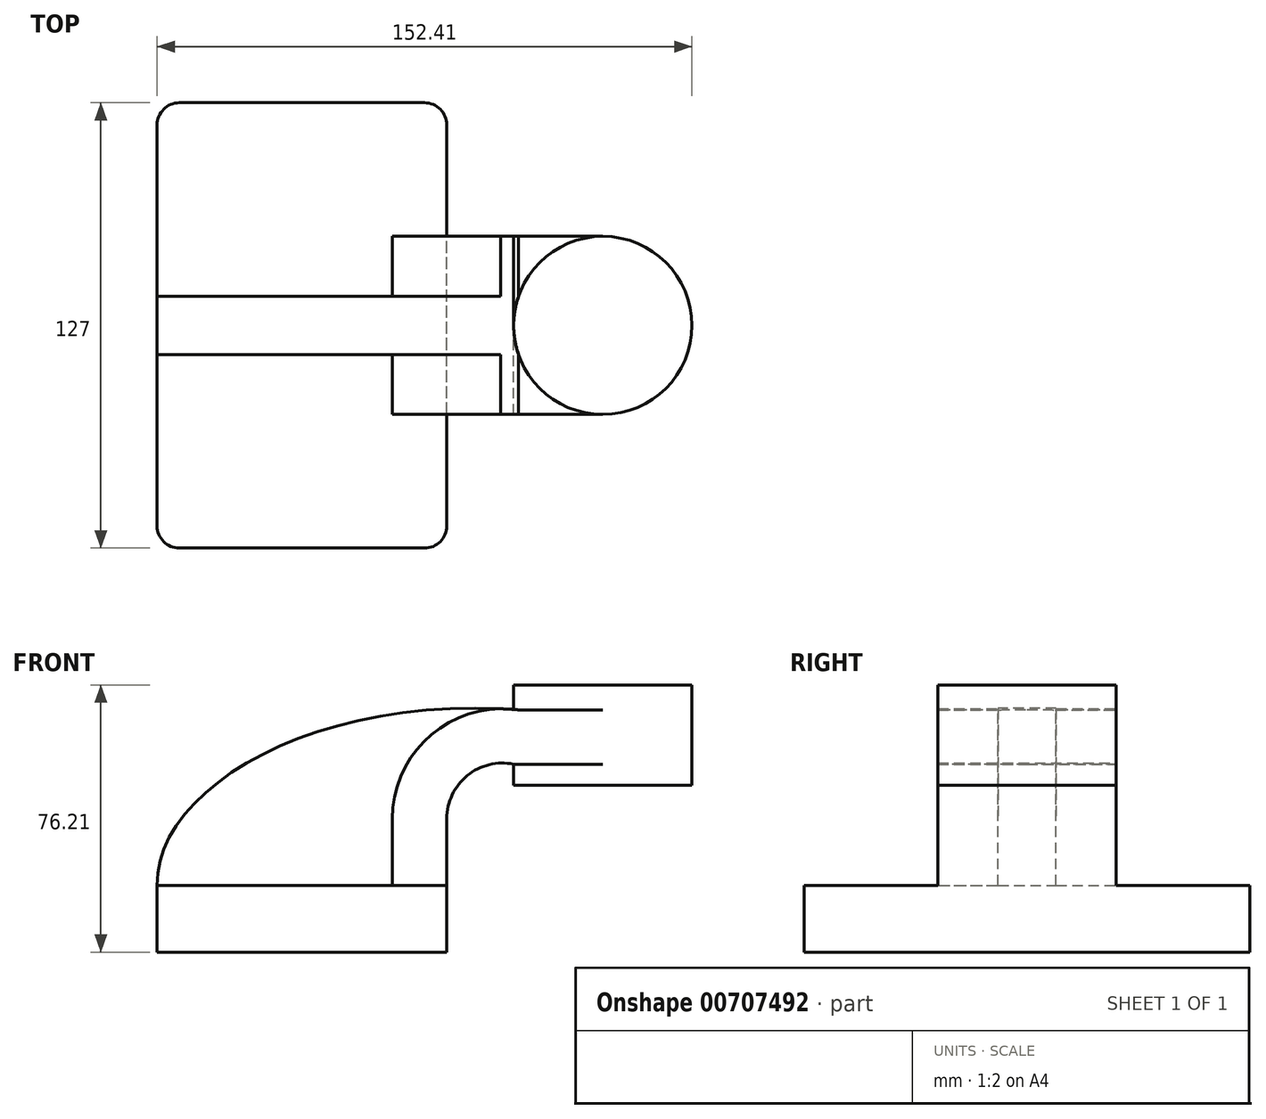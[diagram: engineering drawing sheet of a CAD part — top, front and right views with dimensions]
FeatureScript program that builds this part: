
annotation { "Feature Type Name" : "Feature", "Feature Type Description" : "" }
export const myFeature = defineFeature(function(context is Context, id is Id, definition is map)
    precondition{}
    {
        {
            var Q0;
            Q0=qCreatedBy(makeId("Front.planeOp"),FACE);
            var sketch = newSketch(context, id + "F0", { "sketchPlane" : qUnion([Q0])});
            skLineSegment(sketch, "E0.bottom", {"start": v(41.28, -9.52) * mm, "end": v(-41.28, -9.52) * mm});
            skLineSegment(sketch, "E0.top", {"start": v(41.28, 9.53) * mm, "end": v(-41.28, 9.53) * mm});
            skLineSegment(sketch, "E0.left", {"start": v(41.28, -9.52) * mm, "end": v(41.28, 9.53) * mm});
            skLineSegment(sketch, "E0.right", {"start": v(-41.28, -9.52) * mm, "end": v(-41.28, 9.53) * mm});
            skPoint(sketch, "E0.middle", {"position": v(0, 0) * mm});
            skLineSegment(sketch, "E1.bottom", {"start": v(111.12, 38.1) * mm, "end": v(60.32, 38.1) * mm});
            skLineSegment(sketch, "E1.top", {"start": v(111.12, 66.68) * mm, "end": v(60.32, 66.68) * mm});
            skLineSegment(sketch, "E1.left", {"start": v(111.12, 38.1) * mm, "end": v(111.12, 66.68) * mm});
            skLineSegment(sketch, "E1.right", {"start": v(60.32, 38.1) * mm, "end": v(60.32, 66.68) * mm});
            skPoint(sketch, "E1.middle", {"position": v(85.72, 52.39) * mm});
            skLineSegment(sketch, "E2", {"start": v(41.28, 9.53) * mm, "end": v(41.28, 28.5) * mm});
            skArc(sketch, "E3", {"start": v(41.28, 28.5) * mm, "mid": v(47.1, 40.8) * mm, "end": v(60.32, 44.06) * mm});
            skLineSegment(sketch, "E4", {"start": v(60.32, 44.06) * mm, "end": v(85.72, 44.06) * mm});
            skLineSegment(sketch, "E5", {"start": v(85.73, 66.68) * mm, "end": v(85.73, 38.1) * mm});
            skPoint(sketch, "E6", {"position": v(85.72, 38.1) * mm});
            skLineSegment(sketch, "E7.0", {"start": v(61.62, 59.55) * mm, "end": v(85.72, 59.55) * mm});
            skArc(sketch, "E7.1", {"start": v(25.78, 28.5) * mm, "mid": v(36.61, 52.22) * mm, "end": v(61.62, 59.55) * mm});
            skLineSegment(sketch, "E7.2", {"start": v(25.78, 9.53) * mm, "end": v(25.78, 28.5) * mm});
            skFitSpline(sketch, "E8", {"points": [v(-41.28, 9.52) * mm, v(61.62, 59.55) * mm], "startDerivative": vector(-1.83, 81.78) * mm, "endDerivative": vector(175.47, -13.6) * mm});
            skSolve(sketch);
        }
        {
            var Q0;
            Q0=makeQuery(id+"F0.imprint","IMPRINT",FACE,{"disambiguationData":[TD([[makeQuery(id+"F0.imprint","IMPRINT",EDGE,{"derivedFrom":sQuery(id+"F0.wireOp",EDGE,"E0.bottom")}),-1.0]])]});
            extrude(context, id + "F1", {"entities" : qUnion([Q0]), "endBound" : BoundingType.SYMMETRIC, "depth" : 127 * mm, "offsetDistance" : 25.4 * mm});
        }
        {
            var Q0;
            {var subQ1=sQuery(id+"F0.wireOp",EDGE,"E2");Q0=makeQuery(id+"F0.imprint","IMPRINT",FACE,{"disambiguationData":[TD([[makeQuery(id+"F0.imprint","IMPRINT",EDGE,{"derivedFrom":subQ1}),1.0]])]});}
            var Q1;
            {var subQ2=sQuery(id+"F0.wireOp",EDGE,"E4");Q1=makeQuery(id+"F0.imprint","IMPRINT",FACE,{"disambiguationData":[TD([[makeQuery(id+"F0.imprint","IMPRINT",EDGE,{"derivedFrom":subQ2}),1.0]])]});}
            extrude(context, id + "F2", {"entities" : qUnion([Q0, Q1]), "operationType" : NewBodyOperationType.ADD, "endBound" : BoundingType.SYMMETRIC, "depth" : 50.8 * mm, "offsetDistance" : 25.4 * mm});
        }
        {
            var Q0;
            {var subQ0=sQuery(id+"F0.wireOp",EDGE,"E7.2");Q0=makeQuery(id+"F0.imprint","IMPRINT",FACE,{"disambiguationData":[TD([[makeQuery(id+"F0.imprint","IMPRINT",EDGE,{"derivedFrom":subQ0}),1.0]])]});}
            extrude(context, id + "F3", {"entities" : qUnion([Q0]), "operationType" : NewBodyOperationType.ADD, "endBound" : BoundingType.SYMMETRIC, "depth" : 16.56 * mm, "offsetDistance" : 25.4 * mm});
        }
        {
            var Q0;
            {var subQ0=sQuery(id+"F0.wireOp",EDGE,"E1.left");Q0=makeQuery(id+"F0.imprint","IMPRINT",FACE,{"disambiguationData":[TD([[makeQuery(id+"F0.imprint","IMPRINT",EDGE,{"derivedFrom":subQ0}),1.0]])]});}
            var Q1;
            Q1=sQuery(id+"F0.wireOp",EDGE,"E5");
            revolve(context, id + "F4", {"operationType" : NewBodyOperationType.ADD, "surfaceOperationType" : NewSurfaceOperationType.NEW, "entities" : qUnion([Q0]), "axis" : qUnion([Q1]), "revolveType" : RevolveType.FULL});
        }
        {
            var Q0;
            Q0=makeQuery(id+"F1.opExtrude","CAP_EDGE",EDGE,{"disambiguationData":[OSD([sQuery(id+"F0.wireOp",EDGE,"E0.left")])],"isStart":false});
            var Q1;
            Q1=makeQuery(id+"F1.opExtrude","CAP_EDGE",EDGE,{"disambiguationData":[OSD([sQuery(id+"F0.wireOp",EDGE,"E0.right")])],"isStart":false});
            var Q2;
            Q2=makeQuery(id+"F1.opExtrude","CAP_EDGE",EDGE,{"disambiguationData":[OSD([sQuery(id+"F0.wireOp",EDGE,"E0.right")])],"isStart":true});
            var Q3;
            Q3=makeQuery(id+"F1.opExtrude","CAP_EDGE",EDGE,{"disambiguationData":[OSD([sQuery(id+"F0.wireOp",EDGE,"E0.left")])],"isStart":true});
            fillet(context, id + "F5", {"entities" : qUnion([Q0, Q1, Q2, Q3]), "radius" : 6.35 * mm, "tangentPropagation" : true, "allowEdgeOverflow" : false});
        }
    });
